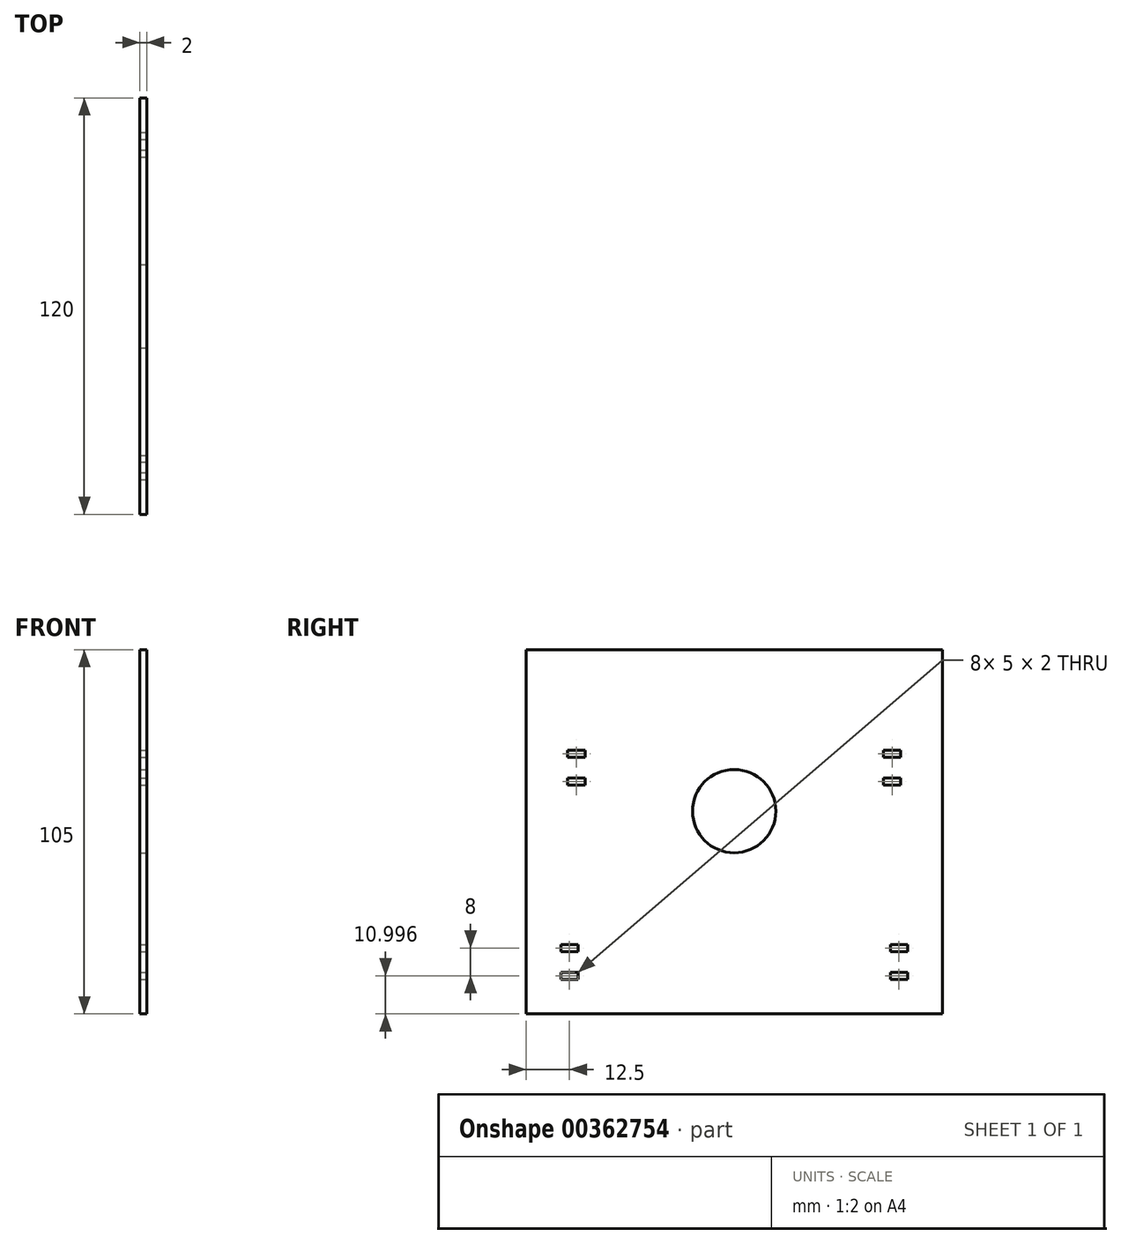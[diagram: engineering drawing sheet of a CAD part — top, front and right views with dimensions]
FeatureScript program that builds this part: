
annotation { "Feature Type Name" : "Feature", "Feature Type Description" : "" }
export const myFeature = defineFeature(function(context is Context, id is Id, definition is map)
    precondition{}
    {
        {
            var Q0;
            Q0=qCreatedBy(makeId("Right.planeOp"),FACE);
            var sketch = newSketch(context, id + "F0", { "sketchPlane" : qUnion([Q0])});
            skLineSegment(sketch, "E0", {"start": v(0, 46.56) * mm, "end": v(60, 46.56) * mm});
            skLineSegment(sketch, "E1", {"start": v(60, 46.56) * mm, "end": v(60, -58.44) * mm});
            skLineSegment(sketch, "E2", {"start": v(60, -58.44) * mm, "end": v(0, -58.44) * mm});
            skLineSegment(sketch, "E3.MirrorCS", {"start": v(0, 46.56) * mm, "end": v(-60, 46.56) * mm});
            skLineSegment(sketch, "E4.MirrorCS", {"start": v(-60, 46.56) * mm, "end": v(-60, -58.44) * mm});
            skLineSegment(sketch, "E5.MirrorCS", {"start": v(-60, -58.44) * mm, "end": v(0, -58.44) * mm});
            skSolve(sketch);
        }
        {
            var Q0;
            Q0=makeQuery(id+"F0.imprint","IMPRINT",FACE,{"disambiguationData":[TD([[makeQuery(id+"F0.imprint","IMPRINT",EDGE,{"derivedFrom":sQuery(id+"F0.wireOp",EDGE,"E0")}),-1.0]])]});
            extrude(context, id + "F1", {"entities" : qUnion([Q0]), "depth" : 2 * mm});
        }
        {
            var Q0;
            Q0=makeQuery(id+"F1.opExtrude","CAP_FACE",FACE,{"disambiguationData":[OSD([sQuery(id+"F0.wireOp",EDGE,"E0"),sQuery(id+"F0.wireOp",EDGE,"E1"),sQuery(id+"F0.wireOp",EDGE,"E2"),sQuery(id+"F0.wireOp",EDGE,"E3.MirrorCS"),sQuery(id+"F0.wireOp",EDGE,"E4.MirrorCS"),sQuery(id+"F0.wireOp",EDGE,"E5.MirrorCS")])],"isStart":false});
            var sketch = newSketch(context, id + "F2", { "sketchPlane" : qUnion([Q0])});
            skLineSegment(sketch, "E6.bottom", {"start": v(-50, -46.44) * mm, "end": v(-45, -46.44) * mm});
            skLineSegment(sketch, "E6.top", {"start": v(-50, -48.44) * mm, "end": v(-45, -48.44) * mm});
            skLineSegment(sketch, "E6.left", {"start": v(-50, -46.44) * mm, "end": v(-50, -48.44) * mm});
            skLineSegment(sketch, "E6.right", {"start": v(-45, -46.44) * mm, "end": v(-45, -48.44) * mm});
            skLineSegment(sketch, "E7.MirrorCS", {"start": v(50, -46.44) * mm, "end": v(45, -46.44) * mm});
            skLineSegment(sketch, "E8.MirrorCS", {"start": v(50, -46.44) * mm, "end": v(50, -48.44) * mm});
            skLineSegment(sketch, "E9.MirrorCS", {"start": v(50, -48.44) * mm, "end": v(45, -48.44) * mm});
            skLineSegment(sketch, "E10.MirrorCS", {"start": v(45, -46.44) * mm, "end": v(45, -48.44) * mm});
            skLineSegment(sketch, "E11", {"start": v(-53.92, -43.44) * mm, "end": v(-41.33, -43.44) * mm, "construction": true});
            skLineSegment(sketch, "E12.MirrorCS", {"start": v(-50, -40.44) * mm, "end": v(-45, -40.44) * mm});
            skLineSegment(sketch, "E13.MirrorCS", {"start": v(-50, -38.44) * mm, "end": v(-45, -38.44) * mm});
            skLineSegment(sketch, "E14.MirrorCS", {"start": v(-45, -40.44) * mm, "end": v(-45, -38.44) * mm});
            skLineSegment(sketch, "E15.MirrorCS", {"start": v(-50, -40.44) * mm, "end": v(-50, -38.44) * mm});
            skLineSegment(sketch, "E16", {"start": v(40.19, -43.44) * mm, "end": v(54.74, -43.44) * mm, "construction": true});
            skLineSegment(sketch, "E17.MirrorCS", {"start": v(50, -40.44) * mm, "end": v(45, -40.44) * mm});
            skLineSegment(sketch, "E18.MirrorCS", {"start": v(45, -40.44) * mm, "end": v(45, -38.44) * mm});
            skLineSegment(sketch, "E19.MirrorCS", {"start": v(50, -38.44) * mm, "end": v(45, -38.44) * mm});
            skLineSegment(sketch, "E20.MirrorCS", {"start": v(50, -40.44) * mm, "end": v(50, -38.44) * mm});
            skSolve(sketch);
        }
        {
            var Q0;
            Q0=qSketchRegion(id+"F2",true);
            extrude(context, id + "F3", {"entities" : qUnion([Q0]), "operationType" : NewBodyOperationType.REMOVE, "oppositeDirection" : true, "depth" : 25 * mm});
        }
        {
            var Q0;
            Q0=makeQuery(id+"F1.opExtrude","CAP_FACE",FACE,{"disambiguationData":[OSD([sQuery(id+"F0.wireOp",EDGE,"E0"),sQuery(id+"F0.wireOp",EDGE,"E1"),sQuery(id+"F0.wireOp",EDGE,"E2"),sQuery(id+"F0.wireOp",EDGE,"E3.MirrorCS"),sQuery(id+"F0.wireOp",EDGE,"E4.MirrorCS"),sQuery(id+"F0.wireOp",EDGE,"E5.MirrorCS")])],"isStart":false});
            var sketch = newSketch(context, id + "F4", { "sketchPlane" : qUnion([Q0])});
            skLineSegment(sketch, "E21.bottom", {"start": v(-48, 9.56) * mm, "end": v(-43, 9.56) * mm});
            skLineSegment(sketch, "E21.top", {"start": v(-48, 7.56) * mm, "end": v(-43, 7.56) * mm});
            skLineSegment(sketch, "E21.left", {"start": v(-48, 9.56) * mm, "end": v(-48, 7.56) * mm});
            skLineSegment(sketch, "E21.right", {"start": v(-43, 9.56) * mm, "end": v(-43, 7.56) * mm});
            skLineSegment(sketch, "E22", {"start": v(-54.64, 12.56) * mm, "end": v(-37.87, 12.56) * mm, "construction": true});
            skLineSegment(sketch, "E23.MirrorCS", {"start": v(-48, 15.56) * mm, "end": v(-48, 17.56) * mm});
            skLineSegment(sketch, "E24.MirrorCS", {"start": v(-48, 17.56) * mm, "end": v(-43, 17.56) * mm});
            skLineSegment(sketch, "E25.MirrorCS", {"start": v(-43, 15.56) * mm, "end": v(-43, 17.56) * mm});
            skLineSegment(sketch, "E26.MirrorCS", {"start": v(-48, 15.56) * mm, "end": v(-43, 15.56) * mm});
            skLineSegment(sketch, "E27.MirrorCS", {"start": v(48, 7.56) * mm, "end": v(43, 7.56) * mm});
            skLineSegment(sketch, "E28.MirrorCS", {"start": v(48, 9.56) * mm, "end": v(48, 7.56) * mm});
            skLineSegment(sketch, "E29.MirrorCS", {"start": v(48, 9.56) * mm, "end": v(43, 9.56) * mm});
            skLineSegment(sketch, "E30.MirrorCS", {"start": v(43, 9.56) * mm, "end": v(43, 7.56) * mm});
            skLineSegment(sketch, "E31.MirrorCS", {"start": v(48, 15.56) * mm, "end": v(43, 15.56) * mm});
            skLineSegment(sketch, "E32.MirrorCS", {"start": v(48, 15.56) * mm, "end": v(48, 17.56) * mm});
            skLineSegment(sketch, "E33.MirrorCS", {"start": v(48, 17.56) * mm, "end": v(43, 17.56) * mm});
            skLineSegment(sketch, "E34.MirrorCS", {"start": v(43, 15.56) * mm, "end": v(43, 17.56) * mm});
            skSolve(sketch);
        }
        {
            var Q0;
            Q0=qSketchRegion(id+"F4",true);
            extrude(context, id + "F5", {"entities" : qUnion([Q0]), "operationType" : NewBodyOperationType.REMOVE, "oppositeDirection" : true, "depth" : 25 * mm});
        }
        {
            var Q0;
            Q0=makeQuery(id+"F1.opExtrude","CAP_FACE",FACE,{"disambiguationData":[OSD([sQuery(id+"F0.wireOp",EDGE,"E0"),sQuery(id+"F0.wireOp",EDGE,"E1"),sQuery(id+"F0.wireOp",EDGE,"E2"),sQuery(id+"F0.wireOp",EDGE,"E3.MirrorCS"),sQuery(id+"F0.wireOp",EDGE,"E4.MirrorCS"),sQuery(id+"F0.wireOp",EDGE,"E5.MirrorCS")])],"isStart":false});
            var sketch = newSketch(context, id + "F6", { "sketchPlane" : qUnion([Q0])});
            skCircle(sketch, "E35", {"center": v(0, 0) * mm, "radius": 12 * mm});
            skSolve(sketch);
        }
        {
            var Q0;
            Q0=makeQuery(id+"F6.imprint","IMPRINT",FACE,{"disambiguationData":[TD([[makeQuery(id+"F6.imprint","IMPRINT",EDGE,{"derivedFrom":sQuery(id+"F6.wireOp",EDGE,"E35")}),1.0]])]});
            extrude(context, id + "F7", {"entities" : qUnion([Q0]), "operationType" : NewBodyOperationType.REMOVE, "oppositeDirection" : true, "depth" : 25 * mm});
        }
    });
